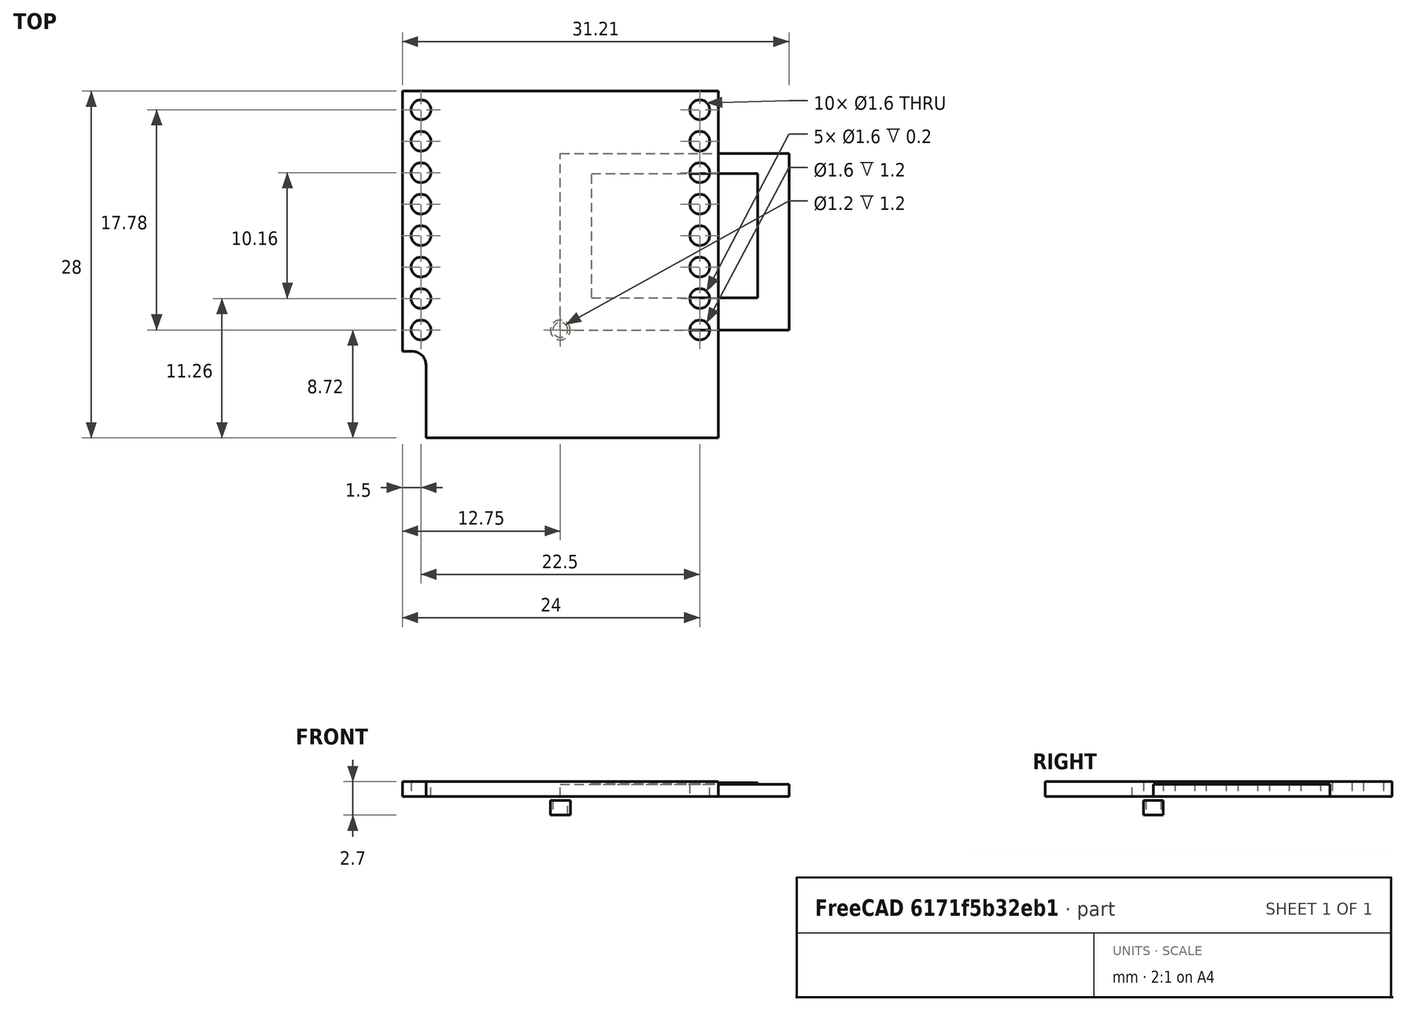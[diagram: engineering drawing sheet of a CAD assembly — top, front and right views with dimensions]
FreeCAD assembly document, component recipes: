
FREECAD ASSEMBLY — COMPONENT RECIPES ("az-oled-066.fcstd")

This assembly document has 17 components, labeled P0..P16 below (a component is one placed body or linked part). 17 of them carry a construction recipe — the FreeCAD feature program that regenerates the part from scratch, quoted from this document or its linked companion documents; the rest are supplied as boundary geometry only. No exploded tour is included for this assembly.
COMPONENT P0 — recipe-attached ("Platine001", modeled in this document).
Construction recipe (the document's own serialized feature program — sketch geometry with constraints, then the solid features built on it; lengths are millimeters unless a unit is written):

FEATURE [PartDesign::FeatureBase] Clone001
  BaseFeature = -> Body
  Suppressed = false
FEATURE [PartDesign::Body] Body002  label="Platine"
  AllowCompound = false
  Group = -> [Clone001]
  Origin = -> Origin002
  Tip = -> Clone001
COMPONENT P1 — recipe-attached ("Via001", modeled in this document).
Construction recipe (the document's own serialized feature program — sketch geometry with constraints, then the solid features built on it; lengths are millimeters unless a unit is written):

FEATURE [PartDesign::FeatureBase] Clone
  BaseFeature = -> Cut
  Placement = pos=(0,0,-1.5) rot=(0,0,1;0rad)
  Suppressed = false
FEATURE [PartDesign::Body] Body001  label="Via"
  AllowCompound = false
  Group = -> [Clone]
  Origin = -> Origin001
  Tip = -> Clone
COMPONENT P2 — same part as P1; its construction recipe is shown at P1.
COMPONENT P3 — same part as P1; its construction recipe is shown at P1.
COMPONENT P4 — same part as P1; its construction recipe is shown at P1.
COMPONENT P5 — same part as P1; its construction recipe is shown at P1.
COMPONENT P6 — same part as P1; its construction recipe is shown at P1.
COMPONENT P7 — same part as P1; its construction recipe is shown at P1.
COMPONENT P8 — same part as P1; its construction recipe is shown at P1.
COMPONENT P9 — same part as P1; its construction recipe is shown at P1.
COMPONENT P10 — same part as P1; its construction recipe is shown at P1.
COMPONENT P11 — same part as P1; its construction recipe is shown at P1.
COMPONENT P12 — same part as P1; its construction recipe is shown at P1.
COMPONENT P13 — same part as P1; its construction recipe is shown at P1.
COMPONENT P14 — same part as P1; its construction recipe is shown at P1.
COMPONENT P15 — same part as P1; its construction recipe is shown at P1.
COMPONENT P16 — same part as P1; its construction recipe is shown at P1.
PROVENANCE & LICENSES
A FreeCAD (.FCStd) document from a public repository crawl; recipes are the document's own serialized feature recipes (and, for linked parts, companion documents' recipes).
License: gpl-3.0.
